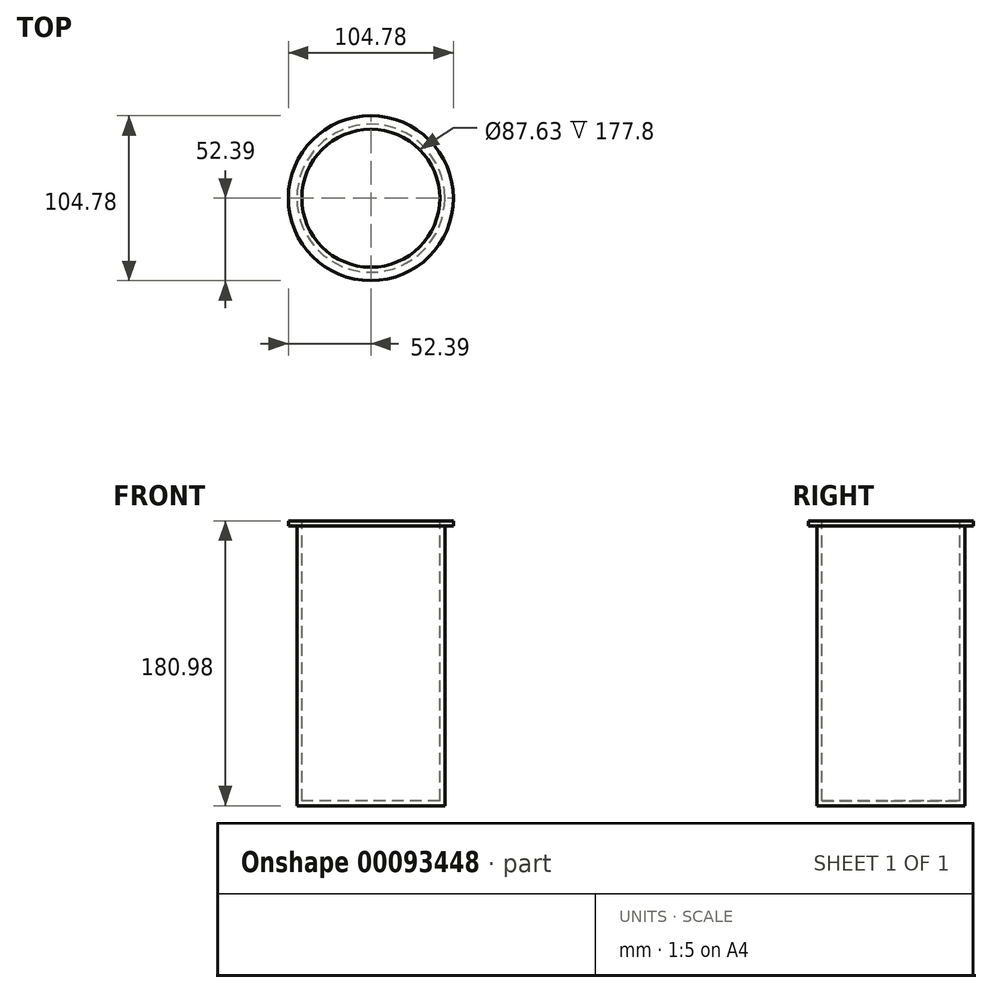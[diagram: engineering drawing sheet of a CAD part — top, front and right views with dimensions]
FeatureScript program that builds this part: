
annotation { "Feature Type Name" : "Feature", "Feature Type Description" : "" }
export const myFeature = defineFeature(function(context is Context, id is Id, definition is map)
    precondition{}
    {
        {
            var Q0;
            Q0=qCreatedBy(makeId("Top.planeOp"),FACE);
            var sketch = newSketch(context, id + "F0", { "sketchPlane" : qUnion([Q0])});
            skCircle(sketch, "E0", {"center": v(0, 0) * mm, "radius": 52.39 * mm});
            skSolve(sketch);
        }
        {
            var Q0;
            Q0=makeQuery(id+"F0.imprint","IMPRINT",FACE,{"disambiguationData":[TD([[makeQuery(id+"F0.imprint","IMPRINT",EDGE,{"derivedFrom":sQuery(id+"F0.wireOp",EDGE,"E0")}),1.0]])]});
            extrude(context, id + "F1", {"entities" : qUnion([Q0]), "depth" : 3.17 * mm});
        }
        {
            var Q0;
            Q0=qCreatedBy(makeId("Top.planeOp"),FACE);
            var sketch = newSketch(context, id + "F2", { "sketchPlane" : qUnion([Q0])});
            skCircle(sketch, "E1", {"center": v(0, 0) * mm, "radius": 47 * mm});
            skSolve(sketch);
        }
        {
            var Q0;
            Q0=makeQuery(id+"F2.imprint","IMPRINT",FACE,{"disambiguationData":[TD([[makeQuery(id+"F2.imprint","IMPRINT",EDGE,{"derivedFrom":sQuery(id+"F2.wireOp",EDGE,"E1")}),1.0]])]});
            extrude(context, id + "F3", {"entities" : qUnion([Q0]), "operationType" : NewBodyOperationType.ADD, "oppositeDirection" : true, "depth" : 177.8 * mm});
        }
        {
            var Q0;
            Q0=qCreatedBy(makeId("Top.planeOp"),FACE);
            cPlane(context, id + "F4", {"entities" : qUnion([Q0]), "cplaneType" : CPlaneType.OFFSET, "offset" : 3.17 * mm, "width" : 152.4 * mm, "height" : 152.4 * mm});
        }
        {
            var Q0;
            Q0=qCreatedBy(id+"F4.planeOp",FACE);
            var sketch = newSketch(context, id + "F5", { "sketchPlane" : qUnion([Q0])});
            skCircle(sketch, "E2", {"center": v(0, 0) * mm, "radius": 43.82 * mm});
            skSolve(sketch);
        }
        {
            var Q0;
            Q0=makeQuery(id+"F5.imprint","IMPRINT",FACE,{"disambiguationData":[TD([[makeQuery(id+"F5.imprint","IMPRINT",EDGE,{"derivedFrom":sQuery(id+"F5.wireOp",EDGE,"E2")}),1.0]])]});
            extrude(context, id + "F6", {"entities" : qUnion([Q0]), "operationType" : NewBodyOperationType.REMOVE, "oppositeDirection" : true, "depth" : 177.8 * mm});
        }
    });
